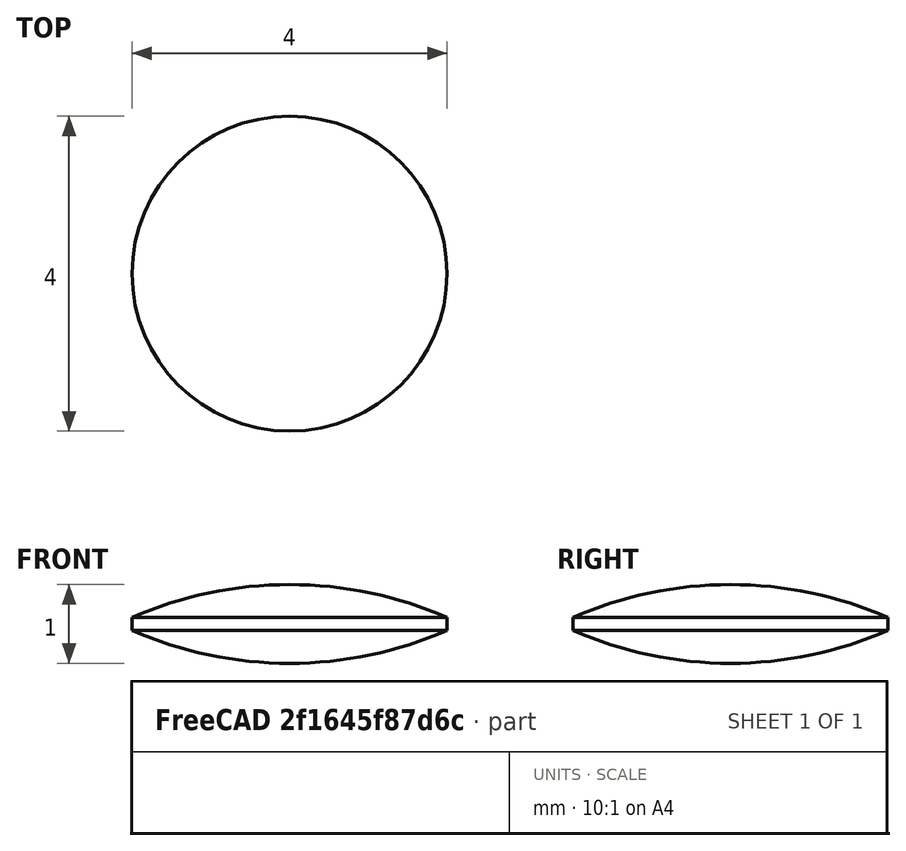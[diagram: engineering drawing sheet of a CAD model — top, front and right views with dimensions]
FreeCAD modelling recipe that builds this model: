
FCSTD DOCUMENT  (FreeCAD 1.1R44874 (Git))
Label: external-file2
License: All rights reserved
LicenseURL: https://en.wikipedia.org/wiki/All_rights_reserved
objects: Part::Sphere×2, Part::Cylinder×1, Part::MultiCommon×1, App::Point×1, App::LinkGroupPython×1, App::Part×1
note: 4 computed .brp shape members not serialized (recipe doc carries the construction recipe); baked Part::Feature solids carry a one-line shape summary decoded from their .brp

FEATURE [Part::Sphere] Sphere
  Angle1 = -90
  Angle2 = 90
  Angle3 = 360
  AttacherType = Attacher::AttachEngine3D
  Placement = pos=(0,0,-2) rot=(0,0,1;0rad)
  Radius = 5
FEATURE [Part::Sphere] Sphere001
  Angle1 = -90
  Angle2 = 90
  Angle3 = 360
  AttacherType = Attacher::AttachEngine3D
  Placement = pos=(0,0,7) rot=(0,0,1;0rad)
  Radius = 5
FEATURE [Part::Cylinder] Cylinder
  Angle = 360
  AttacherType = Attacher::AttachEngine3D
  FirstAngle = 0
  Height = 10
  Placement = pos=(0,0,-3) rot=(0,0,1;0rad)
  Radius = 2
  SecondAngle = 0
FEATURE [Part::MultiCommon] Common
  Behavior = 0
  Refine = true
  Shapes = -> [Sphere,Sphere001,Cylinder]
FEATURE [App::Point] Origin001
  Role = Origin
FEATURE [App::LinkGroupPython] OpticalLensGroup  # WARN: FeaturePython — macro-defined, semantics opaque (R4)
  AbsorptionLength = inf
  ElementList = -> [Common]
  GratingDiffractionOrder = 1
  GratingLinesOrientation = (0,0,1)
  GratingLinesPerMillimeter = 1000
  GratingType = 0
  LinkMode = 0
  ModifyPhiDomain = 0, 2*pi
  ModifyThetaDomain = -pi/2, pi/2
  OpticalType = 1
  Placement = pos=(0,0,-2.5) rot=(0,0,1;0rad)
  PowerPhiDomain = 0, 2*pi
  PowerThetaDomain = -pi/2, pi/2
  RecordHits = false
  Reflectivity = 1
  RefractiveIndex = 1.4
FEATURE [App::Part] Part  label="spherical-lens"
  Group = -> [OpticalLensGroup]
  Origin = -> Origin
